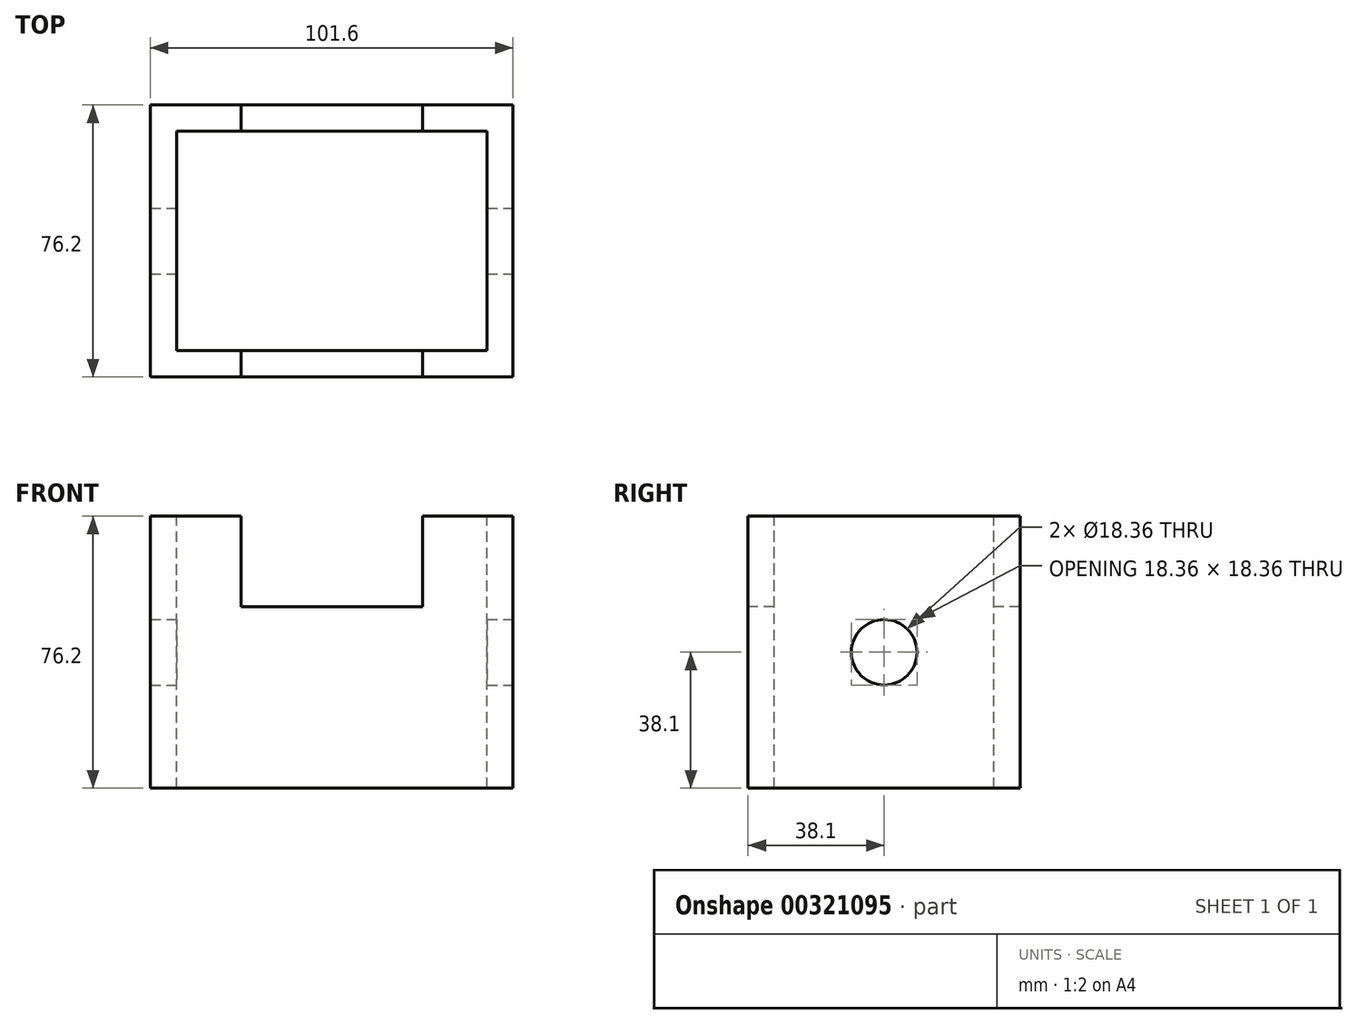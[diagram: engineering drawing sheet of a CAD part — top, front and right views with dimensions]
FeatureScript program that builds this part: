
annotation { "Feature Type Name" : "Feature", "Feature Type Description" : "" }
export const myFeature = defineFeature(function(context is Context, id is Id, definition is map)
    precondition{}
    {
        {
            var Q0;
            Q0=qCreatedBy(makeId("Top.planeOp"),FACE);
            var sketch = newSketch(context, id + "F0", { "sketchPlane" : qUnion([Q0])});
            skLineSegment(sketch, "E0.bottom", {"start": v(-50.8, 38.1) * mm, "end": v(50.8, 38.1) * mm});
            skLineSegment(sketch, "E0.top", {"start": v(-50.8, -38.1) * mm, "end": v(50.8, -38.1) * mm});
            skLineSegment(sketch, "E0.left", {"start": v(-50.8, 38.1) * mm, "end": v(-50.8, -38.1) * mm});
            skLineSegment(sketch, "E0.right", {"start": v(50.8, 38.1) * mm, "end": v(50.8, -38.1) * mm});
            skSolve(sketch);
        }
        {
            var Q0;
            Q0=makeQuery(id+"F0.imprint","IMPRINT",FACE,{"disambiguationData":[TD([[makeQuery(id+"F0.imprint","IMPRINT",EDGE,{"derivedFrom":sQuery(id+"F0.wireOp",EDGE,"E0.bottom")}),-1.0]])]});
            extrude(context, id + "F1", {"entities" : qUnion([Q0]), "endBound" : BoundingType.SYMMETRIC, "depth" : 76.2 * mm});
        }
        {
            var Q0;
            Q0=makeQuery(id+"F1.opExtrude","CAP_FACE",FACE,{"disambiguationData":[OSD([sQuery(id+"F0.wireOp",EDGE,"E0.bottom"),sQuery(id+"F0.wireOp",EDGE,"E0.top"),sQuery(id+"F0.wireOp",EDGE,"E0.left"),sQuery(id+"F0.wireOp",EDGE,"E0.right")])],"isStart":false});
            var sketch = newSketch(context, id + "F2", { "sketchPlane" : qUnion([Q0])});
            skLineSegment(sketch, "E1.0", {"start": v(-43.43, -30.73) * mm, "end": v(43.43, -30.73) * mm});
            skLineSegment(sketch, "E1.1", {"start": v(-43.43, 30.73) * mm, "end": v(-43.43, -30.73) * mm});
            skLineSegment(sketch, "E1.2", {"start": v(-43.43, 30.73) * mm, "end": v(43.43, 30.73) * mm});
            skLineSegment(sketch, "E1.3", {"start": v(43.43, 30.73) * mm, "end": v(43.43, -30.73) * mm});
            skSolve(sketch);
        }
        {
            var Q0;
            Q0=makeQuery(id+"F2.imprint","IMPRINT",FACE,{"disambiguationData":[TD([[makeQuery(id+"F2.imprint","IMPRINT",EDGE,{"derivedFrom":sQuery(id+"F2.wireOp",EDGE,"E1.0")}),1.0]])]});
            extrude(context, id + "F3", {"entities" : qUnion([Q0]), "operationType" : NewBodyOperationType.REMOVE, "endBound" : BoundingType.THROUGH_ALL, "oppositeDirection" : true, "depth" : 25.4 * mm});
        }
        {
            var Q0;
            Q0=makeQuery(id+"F1.opExtrude","SWEPT_FACE",FACE,{"disambiguationData":[OSD([sQuery(id+"F0.wireOp",EDGE,"E0.top")])]});
            var sketch = newSketch(context, id + "F4", { "sketchPlane" : qUnion([Q0])});
            skLineSegment(sketch, "E2.bottom", {"start": v(-25.4, 12.7) * mm, "end": v(25.4, 12.7) * mm});
            skLineSegment(sketch, "E2.top", {"start": v(-25.4, 63.81) * mm, "end": v(25.4, 63.81) * mm});
            skLineSegment(sketch, "E2.left", {"start": v(-25.4, 12.7) * mm, "end": v(-25.4, 63.81) * mm});
            skLineSegment(sketch, "E2.right", {"start": v(25.4, 12.7) * mm, "end": v(25.4, 63.81) * mm});
            skSolve(sketch);
        }
        {
            var Q0;
            {var subQ0=sQuery(id+"F4.wireOp",EDGE,"E2.bottom");Q0=makeQuery(id+"F4.imprint","IMPRINT",FACE,{"disambiguationData":[TD([[makeQuery(id+"F4.imprint","IMPRINT",EDGE,{"derivedFrom":subQ0}),1.0]])]});}
            var Q1;
            {var subQ0=sQuery(id+"F4.wireOp",EDGE,"E2.top");Q1=makeQuery(id+"F4.imprint","IMPRINT",FACE,{"disambiguationData":[TD([[makeQuery(id+"F4.imprint","IMPRINT",EDGE,{"derivedFrom":subQ0}),-1.0]])]});}
            extrude(context, id + "F5", {"entities" : qUnion([Q0, Q1]), "operationType" : NewBodyOperationType.REMOVE, "endBound" : BoundingType.THROUGH_ALL, "oppositeDirection" : true, "depth" : 25.4 * mm});
        }
        {
            var Q0;
            Q0=makeQuery(id+"F1.opExtrude","SWEPT_FACE",FACE,{"disambiguationData":[OSD([sQuery(id+"F0.wireOp",EDGE,"E0.right")])]});
            var sketch = newSketch(context, id + "F6", { "sketchPlane" : qUnion([Q0])});
            skCircle(sketch, "E3", {"center": v(0, 0) * mm, "radius": 9.18 * mm});
            skSolve(sketch);
        }
        {
            var Q0;
            Q0=makeQuery(id+"F6.imprint","IMPRINT",FACE,{"disambiguationData":[TD([[makeQuery(id+"F6.imprint","IMPRINT",EDGE,{"derivedFrom":sQuery(id+"F6.wireOp",EDGE,"E3")}),1.0]])]});
            extrude(context, id + "F7", {"entities" : qUnion([Q0]), "operationType" : NewBodyOperationType.REMOVE, "endBound" : BoundingType.THROUGH_ALL, "oppositeDirection" : true, "depth" : 25.4 * mm});
        }
    });
